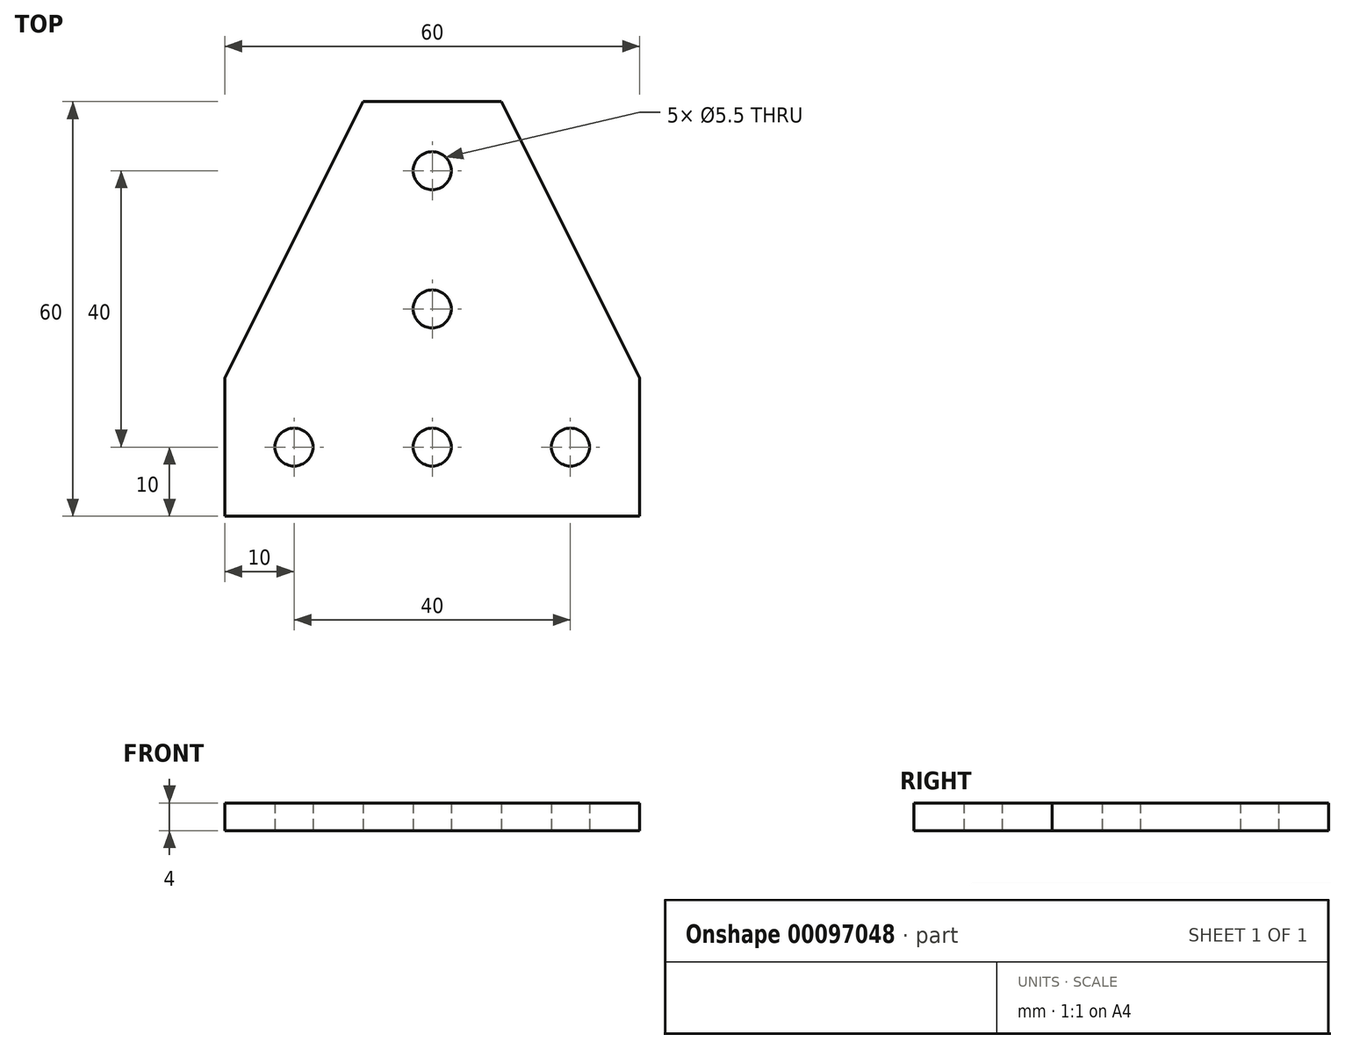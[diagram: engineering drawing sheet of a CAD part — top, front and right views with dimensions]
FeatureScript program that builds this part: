
annotation { "Feature Type Name" : "Feature", "Feature Type Description" : "" }
export const myFeature = defineFeature(function(context is Context, id is Id, definition is map)
    precondition{}
    {
        {
            var Q0;
            Q0=qCreatedBy(makeId("Top.planeOp"),FACE);
            var sketch = newSketch(context, id + "F0", { "sketchPlane" : qUnion([Q0])});
            skLineSegment(sketch, "E0", {"start": v(-30, 0) * mm, "end": v(30, 0) * mm});
            skLineSegment(sketch, "E1", {"start": v(30, 0) * mm, "end": v(30, 20) * mm});
            skLineSegment(sketch, "E2", {"start": v(30, 20) * mm, "end": v(10, 60) * mm});
            skLineSegment(sketch, "E3", {"start": v(10, 60) * mm, "end": v(-10, 60) * mm});
            skLineSegment(sketch, "E4", {"start": v(-10, 60) * mm, "end": v(-30, 20) * mm});
            skLineSegment(sketch, "E5", {"start": v(-30, 20) * mm, "end": v(-30, 0) * mm});
            skCircle(sketch, "E6", {"center": v(-20, 10) * mm, "radius": 2.75 * mm});
            skCircle(sketch, "E7", {"center": v(0, 10) * mm, "radius": 2.75 * mm});
            skCircle(sketch, "E8", {"center": v(20, 10) * mm, "radius": 2.75 * mm});
            skCircle(sketch, "E9", {"center": v(0, 30) * mm, "radius": 2.75 * mm});
            skCircle(sketch, "E10", {"center": v(0, 50) * mm, "radius": 2.75 * mm});
            skSolve(sketch);
        }
        {
            var Q0;
            Q0=qSketchRegion(id+"F0",true);
            extrude(context, id + "F1", {"entities" : qUnion([Q0]), "depth" : 4 * mm});
        }
    });
